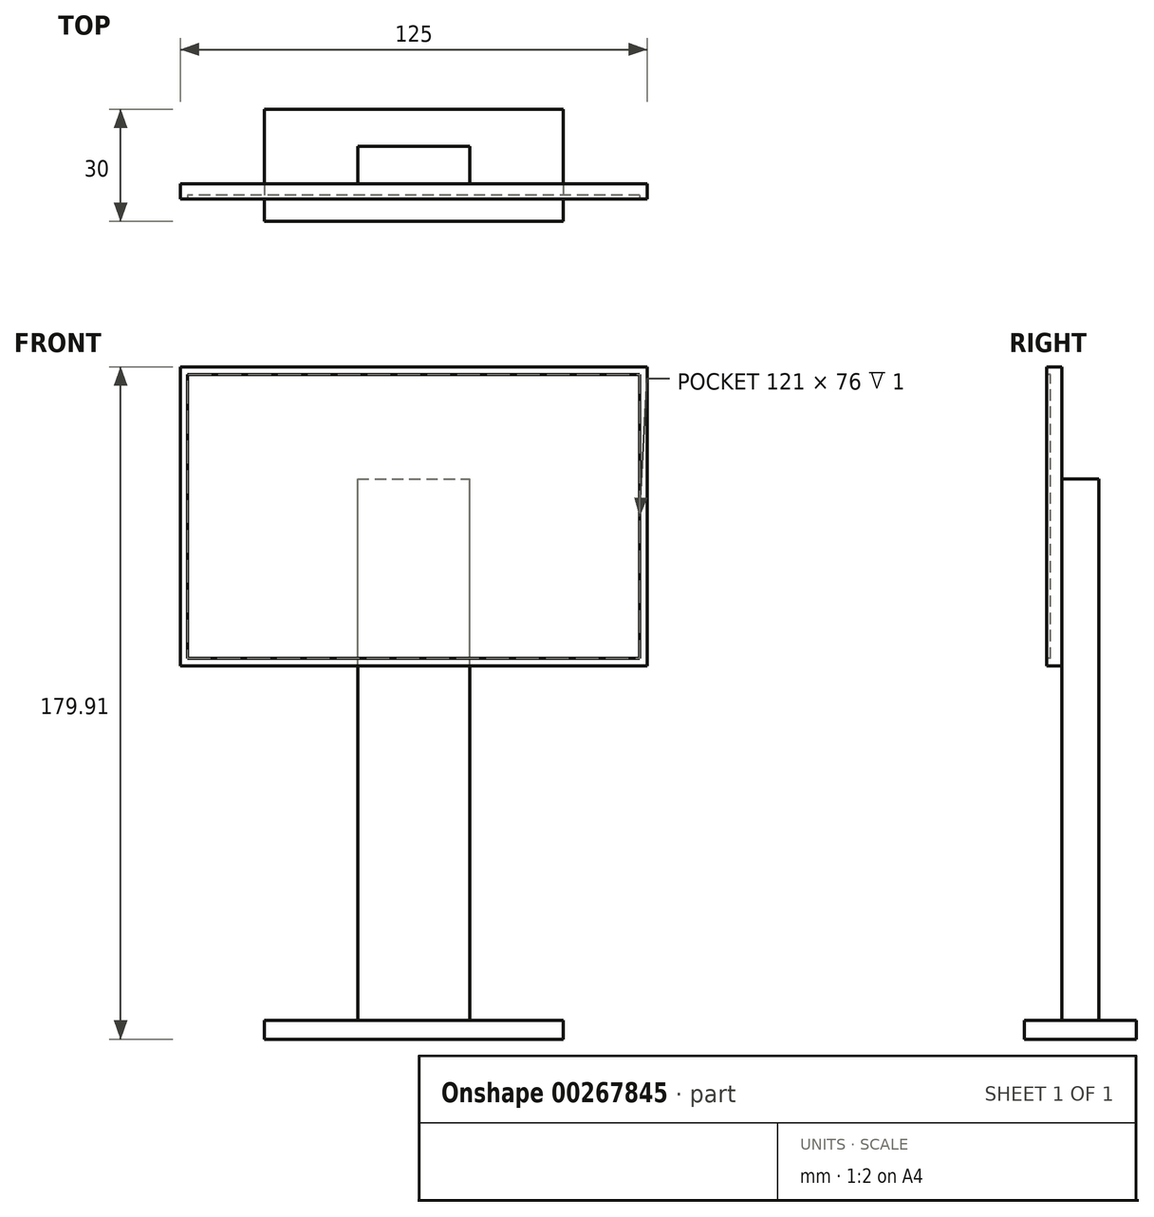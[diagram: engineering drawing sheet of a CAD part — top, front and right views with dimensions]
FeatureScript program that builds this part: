
annotation { "Feature Type Name" : "Feature", "Feature Type Description" : "" }
export const myFeature = defineFeature(function(context is Context, id is Id, definition is map)
    precondition{}
    {
        {
            var Q0;
            Q0=qCreatedBy(makeId("Front.planeOp"),FACE);
            var sketch = newSketch(context, id + "F0", { "sketchPlane" : qUnion([Q0])});
            skLineSegment(sketch, "E0.bottom", {"start": v(62.5, -40) * mm, "end": v(-62.5, -40) * mm});
            skLineSegment(sketch, "E0.top", {"start": v(62.5, 40) * mm, "end": v(-62.5, 40) * mm});
            skLineSegment(sketch, "E0.left", {"start": v(62.5, -40) * mm, "end": v(62.5, 40) * mm});
            skLineSegment(sketch, "E0.right", {"start": v(-62.5, -40) * mm, "end": v(-62.5, 40) * mm});
            skPoint(sketch, "E0.middle", {"position": v(0, 0) * mm});
            skLineSegment(sketch, "E1.0", {"start": v(60.5, 38) * mm, "end": v(-60.5, 38) * mm});
            skLineSegment(sketch, "E1.1", {"start": v(60.5, -38) * mm, "end": v(60.5, 38) * mm});
            skLineSegment(sketch, "E1.2", {"start": v(60.5, -38) * mm, "end": v(-60.5, -38) * mm});
            skLineSegment(sketch, "E1.3", {"start": v(-60.5, -38) * mm, "end": v(-60.5, 38) * mm});
            skSolve(sketch);
        }
        {
            var Q0;
            Q0=makeQuery(id+"F0.imprint","IMPRINT",FACE,{"disambiguationData":[TD([[makeQuery(id+"F0.imprint","IMPRINT",EDGE,{"derivedFrom":sQuery(id+"F0.wireOp",EDGE,"E0.bottom")}),-1.0]])]});
            var Q1;
            Q1=makeQuery(id+"F0.imprint","IMPRINT",FACE,{"disambiguationData":[TD([[makeQuery(id+"F0.imprint","IMPRINT",EDGE,{"derivedFrom":sQuery(id+"F0.wireOp",EDGE,"E1.0")}),1.0]])]});
            extrude(context, id + "F1", {"entities" : qUnion([Q0, Q1]), "depth" : 4 * mm});
        }
        {
            var Q0;
            Q0=makeQuery(id+"F1.opExtrude","CAP_FACE",FACE,{"disambiguationData":[OSD([sQuery(id+"F0.wireOp",EDGE,"E0.bottom"),sQuery(id+"F0.wireOp",EDGE,"E0.top"),sQuery(id+"F0.wireOp",EDGE,"E0.left"),sQuery(id+"F0.wireOp",EDGE,"E0.right")])],"isStart":false});
            var sketch = newSketch(context, id + "F2", { "sketchPlane" : qUnion([Q0])});
            skLineSegment(sketch, "E2.0", {"start": v(60.5, 38) * mm, "end": v(-60.5, 38) * mm});
            skLineSegment(sketch, "E3.0", {"start": v(-60.5, -38) * mm, "end": v(-60.5, 38) * mm});
            skLineSegment(sketch, "E4.0", {"start": v(60.5, -38) * mm, "end": v(60.5, 38) * mm});
            skLineSegment(sketch, "E5.0", {"start": v(60.5, -38) * mm, "end": v(-60.5, -38) * mm});
            skSolve(sketch);
        }
        {
            var Q0;
            Q0=makeQuery(id+"F2.imprint","IMPRINT",FACE,{"disambiguationData":[TD([[makeQuery(id+"F2.imprint","IMPRINT",EDGE,{"derivedFrom":sQuery(id+"F2.wireOp",EDGE,"E2.0")}),1.0]])]});
            extrude(context, id + "F3", {"entities" : qUnion([Q0]), "operationType" : NewBodyOperationType.REMOVE, "oppositeDirection" : true, "depth" : 1 * mm});
        }
        {
            var Q0;
            Q0=makeQuery(id+"F0.imprint","IMPRINT",FACE,{"disambiguationData":[TD([[makeQuery(id+"F0.imprint","IMPRINT",EDGE,{"derivedFrom":sQuery(id+"F0.wireOp",EDGE,"E1.0")}),1.0]])]});
            var sketch = newSketch(context, id + "F4", { "sketchPlane" : qUnion([Q0])});
            skLineSegment(sketch, "E6", {"start": v(0, 92.45) * mm, "end": v(0, -122.62) * mm, "construction": true});
            skLineSegment(sketch, "E7.bottom", {"start": v(-15, -139.91) * mm, "end": v(15, -139.91) * mm});
            skLineSegment(sketch, "E7.top", {"start": v(-15, 10.09) * mm, "end": v(15, 10.09) * mm});
            skLineSegment(sketch, "E7.left", {"start": v(-15, -139.91) * mm, "end": v(-15, 10.09) * mm});
            skLineSegment(sketch, "E7.right", {"start": v(15, -139.91) * mm, "end": v(15, 10.09) * mm});
            skPoint(sketch, "E7.middle", {"position": v(0, -64.91) * mm});
            skSolve(sketch);
        }
        {
            var Q0;
            {var subQ0=sQuery(id+"F4.wireOp",EDGE,"E7.bottom");Q0=makeQuery(id+"F4.imprint","IMPRINT",FACE,{"disambiguationData":[TD([[makeQuery(id+"F4.imprint","IMPRINT",EDGE,{"derivedFrom":subQ0}),1.0]])]});}
            var Q1;
            {var subQ0=sQuery(id+"F4.wireOp",EDGE,"E7.top");Q1=makeQuery(id+"F4.imprint","IMPRINT",FACE,{"disambiguationData":[TD([[makeQuery(id+"F4.imprint","IMPRINT",EDGE,{"derivedFrom":subQ0}),-1.0]])]});}
            extrude(context, id + "F5", {"entities" : qUnion([Q0, Q1]), "operationType" : NewBodyOperationType.ADD, "oppositeDirection" : true, "depth" : 10 * mm});
        }
        {
            var Q0;
            Q0=makeQuery(id+"F5.opExtrude","SWEPT_FACE",FACE,{"disambiguationData":[OSD([sQuery(id+"F4.wireOp",EDGE,"E7.bottom")])]});
            var sketch = newSketch(context, id + "F6", { "sketchPlane" : qUnion([Q0])});
            skLineSegment(sketch, "E8.bottom", {"start": v(40, -20) * mm, "end": v(-40, -20) * mm});
            skLineSegment(sketch, "E8.top", {"start": v(40, 10) * mm, "end": v(-40, 10) * mm});
            skLineSegment(sketch, "E8.left", {"start": v(40, -20) * mm, "end": v(40, 10) * mm});
            skLineSegment(sketch, "E8.right", {"start": v(-40, -20) * mm, "end": v(-40, 10) * mm});
            skPoint(sketch, "E8.middle", {"position": v(0, -5) * mm});
            skPoint(sketch, "E8.middle.positionSnap0", {"position": v(-15, -5) * mm});
            skPoint(sketch, "E8.centerSnap0", {"position": v(-15, -5) * mm});
            skSolve(sketch);
        }
        {
            var Q0;
            Q0=makeQuery(id+"F6.imprint","IMPRINT",FACE,{"disambiguationData":[TD([[makeQuery(id+"F6.imprint","IMPRINT",EDGE,{"derivedFrom":sQuery(id+"F6.wireOp",EDGE,"E8.bottom")}),-1.0]])]});
            extrude(context, id + "F7", {"entities" : qUnion([Q0]), "operationType" : NewBodyOperationType.ADD, "oppositeDirection" : true, "depth" : 5 * mm});
        }
    });
